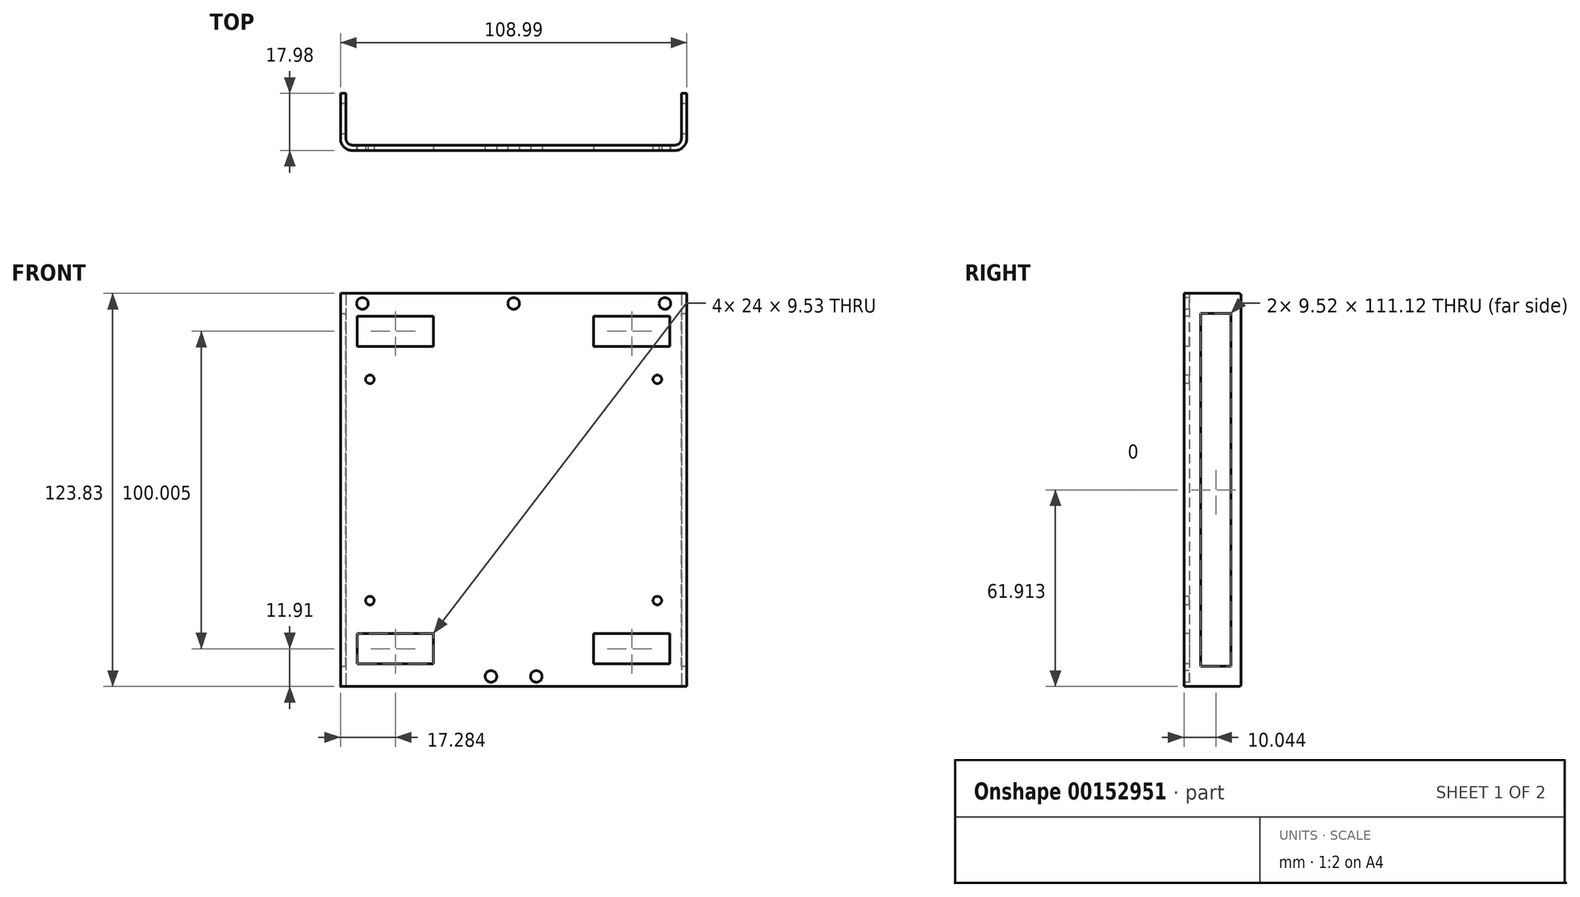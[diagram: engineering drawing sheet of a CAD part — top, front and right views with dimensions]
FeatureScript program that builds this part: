
annotation { "Feature Type Name" : "Feature", "Feature Type Description" : "" }
export const myFeature = defineFeature(function(context is Context, id is Id, definition is map)
    precondition{}
    {
        {
            var Q0;
            Q0=qCreatedBy(makeId("Top.planeOp"),FACE);
            var sketch = newSketch(context, id + "F0", { "sketchPlane" : qUnion([Q0])});
            skLineSegment(sketch, "E0.bottom", {"start": v(0, 0) * mm, "end": v(-105.57, 0) * mm});
            skLineSegment(sketch, "E0.top", {"start": v(1.7, -1.7) * mm, "end": v(-107.28, -1.7) * mm});
            skLineSegment(sketch, "E1.top", {"start": v(-105.57, 16.27) * mm, "end": v(-107.28, 16.27) * mm});
            skLineSegment(sketch, "E1.left", {"start": v(-105.57, 0) * mm, "end": v(-105.57, 16.27) * mm});
            skLineSegment(sketch, "E1.right", {"start": v(-107.28, -1.7) * mm, "end": v(-107.28, 16.27) * mm});
            skLineSegment(sketch, "E2.top", {"start": v(0, 16.27) * mm, "end": v(1.7, 16.27) * mm});
            skLineSegment(sketch, "E2.left", {"start": v(0, 0) * mm, "end": v(0, 16.27) * mm});
            skLineSegment(sketch, "E2.right", {"start": v(1.7, -1.7) * mm, "end": v(1.7, 16.27) * mm});
            skLineSegment(sketch, "E3", {"start": v(-52.78, 0) * mm, "end": v(-52.78, -1.7) * mm, "construction": true});
            skSolve(sketch);
        }
        {
            var Q0;
            Q0=qSketchRegion(id+"F0",true);
            extrude(context, id + "F1", {"entities" : qUnion([Q0]), "depth" : 123.82 * mm});
        }
        {
            var Q0;
            Q0=makeQuery(id+"F1.opExtrude","SWEPT_FACE",FACE,{"disambiguationData":[OSD([sQuery(id+"F0.wireOp",EDGE,"E2.right")])]});
            var sketch = newSketch(context, id + "F2", { "sketchPlane" : qUnion([Q0])});
            skLineSegment(sketch, "E4.bottom", {"start": v(13.1, 117.48) * mm, "end": v(3.57, 117.48) * mm});
            skLineSegment(sketch, "E4.top", {"start": v(13.1, 6.35) * mm, "end": v(3.57, 6.35) * mm});
            skLineSegment(sketch, "E4.left", {"start": v(13.1, 117.48) * mm, "end": v(13.1, 6.35) * mm});
            skLineSegment(sketch, "E4.right", {"start": v(3.57, 117.48) * mm, "end": v(3.57, 6.35) * mm});
            skLineSegment(sketch, "E5", {"start": v(13.1, 61.91) * mm, "end": v(16.27, 61.91) * mm, "construction": true});
            skLineSegment(sketch, "E6", {"start": v(8.33, 6.35) * mm, "end": v(8.33, 0) * mm, "construction": true});
            skSolve(sketch);
        }
        {
            var Q0;
            Q0=qSketchRegion(id+"F2",true);
            var Q1;
            Q1=makeQuery(id+"F1.opExtrude","SWEPT_FACE",FACE,{"disambiguationData":[OSD([sQuery(id+"F0.wireOp",EDGE,"E1.right")])]});
            extrude(context, id + "F3", {"entities" : qUnion([Q0]), "operationType" : NewBodyOperationType.REMOVE, "endBound" : BoundingType.UP_TO_SURFACE, "oppositeDirection" : true, "endBoundEntityFace" : qUnion([Q1]), "depth" : 25.4 * mm});
        }
        {
            var Q0;
            Q0=makeQuery(id+"F1.opExtrude","SWEPT_EDGE",EDGE,{"disambiguationData":[OSD([sQuery(id+"F0.wireOp",EDGE,"E0.top"),sQuery(id+"F0.wireOp",EDGE,"E2.right")])]});
            var Q1;
            Q1=makeQuery(id+"F1.opExtrude","SWEPT_EDGE",EDGE,{"disambiguationData":[OSD([sQuery(id+"F0.wireOp",EDGE,"E0.top"),sQuery(id+"F0.wireOp",EDGE,"E1.right")])]});
            var Q2;
            Q2=makeQuery(id+"FqNnmMD7oaRdpTN_1.opExtrude","CAP_EDGE",EDGE,{"disambiguationData":[OSD([sQuery(id+"FY5sMr6MULj5lJw_1.wireOp",EDGE,"W42EfhJi-fDm4-L9BW-folL-irsYfDskuzBk.top")])],"isStart":false});
            fillet(context, id + "F4", {"entities" : qUnion([Q0, Q1, Q2]), "radius" : 3.7 * mm, "tangentPropagation" : true, "allowEdgeOverflow" : false});
        }
        {
            var Q0;
            Q0=makeQuery(id+"F1.opExtrude","SWEPT_EDGE",EDGE,{"disambiguationData":[OSD([sQuery(id+"F0.wireOp",EDGE,"E0.bottom"),sQuery(id+"F0.wireOp",EDGE,"E2.left")])]});
            var Q1;
            Q1=makeQuery(id+"F1.opExtrude","SWEPT_EDGE",EDGE,{"disambiguationData":[OSD([sQuery(id+"F0.wireOp",EDGE,"E0.bottom"),sQuery(id+"F0.wireOp",EDGE,"E1.left")])]});
            var Q2;
            Q2=makeQuery(id+"FINw0yXB7tfJ6ph_1.opExtrude","CAP_EDGE",EDGE,{"disambiguationData":[OSD([sQuery(id+"FXTh39mUIuS7Wju_1.wireOp",EDGE,"hp9PxWrt-gqSh-sbC0-0nHm-23euh1xvblPI.top")])],"isStart":true});
            fillet(context, id + "F5", {"entities" : qUnion([Q0, Q1, Q2]), "radius" : 1.98 * mm, "tangentPropagation" : true, "allowEdgeOverflow" : false});
        }
        {
            var Q0;
            Q0=makeQuery(id+"FqNnmMD7oaRdpTN_1.boolean.opBoolean","MERGE",FACE,{"derivedFrom":[makeQuery(id+"F1.opExtrude","SWEPT_FACE",FACE,{"disambiguationData":[OSD([sQuery(id+"F0.wireOp",EDGE,"E0.top")])]}),makeQuery(id+"FqNnmMD7oaRdpTN_1.opExtrude","SWEPT_FACE",FACE,{"disambiguationData":[OSD([sQuery(id+"FY5sMr6MULj5lJw_1.wireOp",EDGE,"W42EfhJi-fDm4-L9BW-folL-irsYfDskuzBk.top")])]})]});
            var sketch = newSketch(context, id + "F6", { "sketchPlane" : qUnion([Q0])});
            skLineSegment(sketch, "E7", {"start": v(-52.78, 123.83) * mm, "end": v(-52.78, 120.65) * mm, "construction": true});
            skLineSegment(sketch, "E8", {"start": v(-103.58, 120.65) * mm, "end": v(-100.4, 120.65) * mm, "construction": true});
            skLineSegment(sketch, "E9", {"start": v(-100.4, 120.65) * mm, "end": v(-5.16, 120.65) * mm, "construction": true});
            skLineSegment(sketch, "E10", {"start": v(-5.16, 120.65) * mm, "end": v(-1.98, 120.65) * mm, "construction": true});
            skCircle(sketch, "E11", {"center": v(-52.78, 120.65) * mm, "radius": 1.83 * mm});
            skCircle(sketch, "E12", {"center": v(-5.16, 120.65) * mm, "radius": 1.83 * mm});
            skCircle(sketch, "E13", {"center": v(-100.4, 120.65) * mm, "radius": 1.83 * mm});
            skLineSegment(sketch, "E14", {"start": v(-52.78, 0) * mm, "end": v(-52.78, 3.17) * mm, "construction": true});
            skLineSegment(sketch, "E15", {"start": v(-45.64, 3.17) * mm, "end": v(-59.93, 3.17) * mm, "construction": true});
            skCircle(sketch, "E16", {"center": v(-45.64, 3.17) * mm, "radius": 1.83 * mm});
            skCircle(sketch, "E17", {"center": v(-59.93, 3.17) * mm, "radius": 1.83 * mm});
            skLineSegment(sketch, "E18.bottom", {"start": v(-102, 116.68) * mm, "end": v(-78, 116.68) * mm});
            skLineSegment(sketch, "E18.top", {"start": v(-102, 107.15) * mm, "end": v(-78, 107.15) * mm});
            skLineSegment(sketch, "E18.left", {"start": v(-102, 116.68) * mm, "end": v(-102, 107.15) * mm});
            skLineSegment(sketch, "E18.right", {"start": v(-78, 116.68) * mm, "end": v(-78, 107.15) * mm});
            skLineSegment(sketch, "E19.bottom", {"start": v(-102, 16.68) * mm, "end": v(-78, 16.68) * mm});
            skLineSegment(sketch, "E19.top", {"start": v(-102, 7.14) * mm, "end": v(-78, 7.14) * mm});
            skLineSegment(sketch, "E19.left", {"start": v(-102, 16.68) * mm, "end": v(-102, 7.14) * mm});
            skLineSegment(sketch, "E19.right", {"start": v(-78, 16.68) * mm, "end": v(-78, 7.14) * mm});
            skLineSegment(sketch, "E20.bottom", {"start": v(-27.57, 116.68) * mm, "end": v(-3.57, 116.68) * mm});
            skLineSegment(sketch, "E20.top", {"start": v(-27.57, 107.15) * mm, "end": v(-3.57, 107.15) * mm});
            skLineSegment(sketch, "E20.left", {"start": v(-27.57, 116.68) * mm, "end": v(-27.57, 107.15) * mm});
            skLineSegment(sketch, "E20.right", {"start": v(-3.57, 116.68) * mm, "end": v(-3.57, 107.15) * mm});
            skLineSegment(sketch, "E21.bottom", {"start": v(-27.57, 7.14) * mm, "end": v(-3.57, 7.14) * mm});
            skLineSegment(sketch, "E21.top", {"start": v(-27.57, 16.68) * mm, "end": v(-3.57, 16.68) * mm});
            skLineSegment(sketch, "E21.left", {"start": v(-27.57, 7.14) * mm, "end": v(-27.57, 16.68) * mm});
            skLineSegment(sketch, "E21.right", {"start": v(-3.57, 7.14) * mm, "end": v(-3.57, 16.68) * mm});
            skLineSegment(sketch, "E22.bottom", {"start": v(-78, 16.68) * mm, "end": v(-27.57, 16.68) * mm, "construction": true});
            skLineSegment(sketch, "E22.top", {"start": v(-78, 107.15) * mm, "end": v(-27.57, 107.15) * mm, "construction": true});
            skLineSegment(sketch, "E22.left", {"start": v(-78, 16.68) * mm, "end": v(-78, 107.15) * mm, "construction": true});
            skLineSegment(sketch, "E22.right", {"start": v(-27.57, 16.68) * mm, "end": v(-27.57, 107.15) * mm, "construction": true});
            skPoint(sketch, "E22.middle", {"position": v(-52.78, 61.91) * mm});
            skLineSegment(sketch, "E23", {"start": v(-103.58, 61.91) * mm, "end": v(-1.98, 61.91) * mm, "construction": true});
            skLineSegment(sketch, "E24", {"start": v(-102, 7.14) * mm, "end": v(-103.58, 7.14) * mm, "construction": true});
            skLineSegment(sketch, "E25", {"start": v(-78, 7.14) * mm, "end": v(-78, 3.18) * mm, "construction": true});
            skLineSegment(sketch, "E26", {"start": v(-59.93, 3.17) * mm, "end": v(-78, 3.17) * mm, "construction": true});
            skLineSegment(sketch, "E27.bottom", {"start": v(-98.03, 96.75) * mm, "end": v(-7.54, 96.75) * mm, "construction": true});
            skLineSegment(sketch, "E27.top", {"start": v(-98.03, 27.07) * mm, "end": v(-7.54, 27.07) * mm, "construction": true});
            skLineSegment(sketch, "E27.left", {"start": v(-98.03, 96.75) * mm, "end": v(-98.03, 27.07) * mm, "construction": true});
            skLineSegment(sketch, "E27.right", {"start": v(-7.54, 96.75) * mm, "end": v(-7.54, 27.07) * mm, "construction": true});
            skLineSegment(sketch, "E28", {"start": v(-102, 107.15) * mm, "end": v(-102, 96.75) * mm, "construction": true});
            skLineSegment(sketch, "E29", {"start": v(-102, 96.75) * mm, "end": v(-98.03, 96.75) * mm, "construction": true});
            skPoint(sketch, "E30", {"position": v(-102, 111.91) * mm});
            skCircle(sketch, "E31", {"center": v(-98.03, 96.75) * mm, "radius": 1.35 * mm});
            skCircle(sketch, "E32", {"center": v(-98.03, 27.07) * mm, "radius": 1.35 * mm});
            skCircle(sketch, "E33", {"center": v(-7.54, 27.07) * mm, "radius": 1.35 * mm});
            skCircle(sketch, "E34", {"center": v(-7.54, 96.75) * mm, "radius": 1.35 * mm});
            skPoint(sketch, "E35", {"position": v(-102, 11.91) * mm});
            skSolve(sketch);
        }
        {
            var Q0;
            Q0=qSketchRegion(id+"F6",true);
            var Q1;
            Q1=makeQuery(id+"FqNnmMD7oaRdpTN_1.boolean.opBoolean","MERGE",FACE,{"derivedFrom":[makeQuery(id+"F1.opExtrude","SWEPT_FACE",FACE,{"disambiguationData":[OSD([sQuery(id+"F0.wireOp",EDGE,"E0.bottom")])]}),makeQuery(id+"FqNnmMD7oaRdpTN_1.opExtrude","SWEPT_FACE",FACE,{"disambiguationData":[OSD([sQuery(id+"FY5sMr6MULj5lJw_1.wireOp",EDGE,"W42EfhJi-fDm4-L9BW-folL-irsYfDskuzBk.bottom")])]})]});
            extrude(context, id + "F7", {"entities" : qUnion([Q0]), "operationType" : NewBodyOperationType.REMOVE, "endBound" : BoundingType.UP_TO_SURFACE, "oppositeDirection" : true, "endBoundEntityFace" : qUnion([Q1]), "depth" : 25.4 * mm});
        }
        {
            var Q0;
            Q0=makeQuery(id+"F1.opExtrude","CAP_EDGE",EDGE,{"disambiguationData":[OSD([sQuery(id+"F0.wireOp",EDGE,"E1.top")])],"isStart":false});
            var Q1;
            Q1=makeQuery(id+"F1.opExtrude","CAP_EDGE",EDGE,{"disambiguationData":[OSD([sQuery(id+"F0.wireOp",EDGE,"E2.top")])],"isStart":false});
            var Q2;
            Q2=makeQuery(id+"F1.opExtrude","CAP_EDGE",EDGE,{"disambiguationData":[OSD([sQuery(id+"F0.wireOp",EDGE,"E2.top")])],"isStart":true});
            var Q3;
            Q3=makeQuery(id+"F1.opExtrude","CAP_EDGE",EDGE,{"disambiguationData":[OSD([sQuery(id+"F0.wireOp",EDGE,"E1.top")])],"isStart":true});
            fillet(context, id + "F8", {"entities" : qUnion([Q0, Q1, Q2, Q3]), "radius" : 0.76 * mm, "tangentPropagation" : true, "allowEdgeOverflow" : false});
        }
    });
